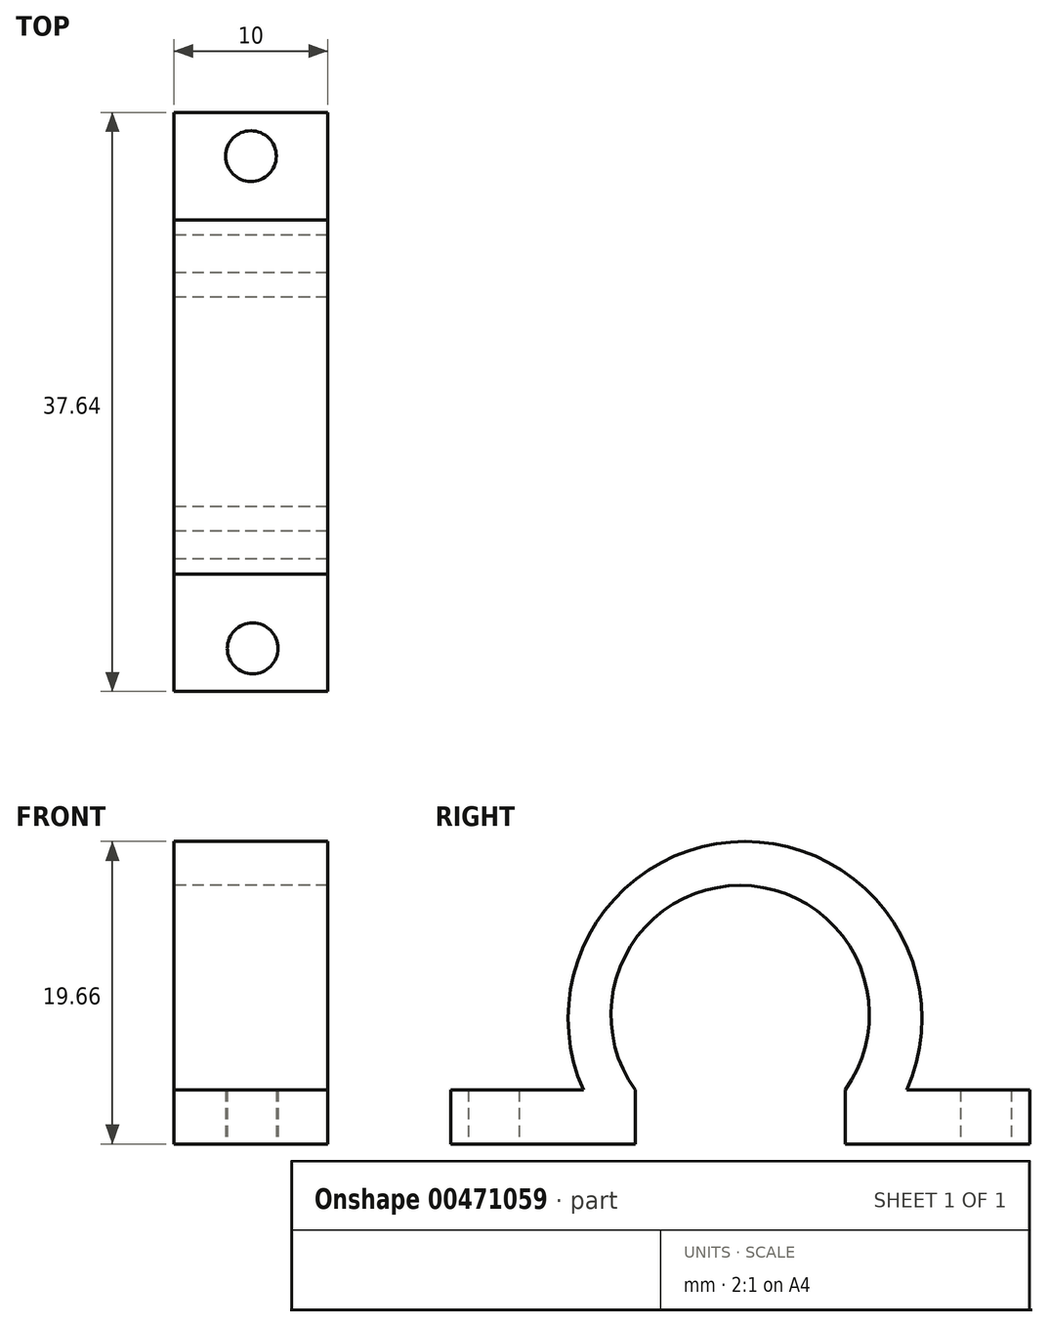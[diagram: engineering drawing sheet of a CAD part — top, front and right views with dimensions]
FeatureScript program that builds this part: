
annotation { "Feature Type Name" : "Feature", "Feature Type Description" : "" }
export const myFeature = defineFeature(function(context is Context, id is Id, definition is map)
    precondition{}
    {
        {
            var Q0;
            Q0=qCreatedBy(makeId("Right.planeOp"),FACE);
            var sketch = newSketch(context, id + "F0", { "sketchPlane" : qUnion([Q0])});
            skArc(sketch, "E0", {"start": v(-9.16, 19.45) * mm, "mid": v(-15.98, 32.75) * mm, "end": v(-22.8, 19.45) * mm});
            skLineSegment(sketch, "E1", {"start": v(-9.16, 15.95) * mm, "end": v(2.84, 15.95) * mm});
            skLineSegment(sketch, "E2", {"start": v(-34.8, 15.95) * mm, "end": v(-22.8, 15.95) * mm});
            skLineSegment(sketch, "E3", {"start": v(2.84, 15.95) * mm, "end": v(2.84, 19.45) * mm});
            skLineSegment(sketch, "E4", {"start": v(2.84, 19.45) * mm, "end": v(-9.16, 19.45) * mm});
            skLineSegment(sketch, "E5", {"start": v(-34.8, 19.45) * mm, "end": v(-34.8, 15.95) * mm});
            skLineSegment(sketch, "E6.trimOffspring", {"start": v(-22.8, 19.45) * mm, "end": v(-34.8, 19.45) * mm});
            skLineSegment(sketch, "E7", {"start": v(-22.8, 19.45) * mm, "end": v(-22.8, 15.95) * mm});
            skLineSegment(sketch, "E8", {"start": v(-9.16, 19.45) * mm, "end": v(-9.16, 15.95) * mm});
            skArc(sketch, "E9", {"start": v(-5.15, 19.45) * mm, "mid": v(-15.66, 35.6) * mm, "end": v(-26.18, 19.45) * mm});
            skSolve(sketch);
        }
        {
            var Q0;
            Q0 = qSketchRegion(id + "F0", true);
            extrude(context, id + "F1", {"entities" : qUnion([Q0]), "depth" : 10 * mm, "offsetDistance" : 25 * mm});
        }
        {
            var Q0;
            Q0=qCreatedBy(makeId("Top.planeOp"),FACE);
            var sketch = newSketch(context, id + "F2", { "sketchPlane" : qUnion([Q0])});
            skCircle(sketch, "E10", {"center": v(5.12, -32) * mm, "radius": 1.6 * mm});
            skCircle(sketch, "E11", {"center": v(5, 0) * mm, "radius": 1.6 * mm});
            skSolve(sketch);
        }
        {
            var Q0;
            Q0=sQuery(id+"F2.wireOp",VERTEX,"E10.center");
            var Q1;
            Q1=makeQuery(id+"F1.opExtrude","SWEPT_BODY",BODY,{"disambiguationData":[OSD([sQuery(id+"F0.wireOp",EDGE,"E0"),sQuery(id+"F0.wireOp",EDGE,"E1"),sQuery(id+"F0.wireOp",EDGE,"E2"),sQuery(id+"F0.wireOp",EDGE,"E3"),sQuery(id+"F0.wireOp",EDGE,"E4"),sQuery(id+"F0.wireOp",EDGE,"E5"),sQuery(id+"F0.wireOp",EDGE,"E6.trimOffspring"),sQuery(id+"F0.wireOp",EDGE,"E7"),sQuery(id+"F0.wireOp",EDGE,"E8"),sQuery(id+"F0.wireOp",EDGE,"E9")])]});
            hole(context, id + "F3", {"style" : HoleStyle.SIMPLE, "endStyle" : HoleEndStyle.THROUGH, "oppositeDirection" : true, "holeDiameter" : 3.3 * mm, "isTappedThrough" : true, "tappedDepth" : 12 * mm, "tapClearance" : 3, "locations" : qUnion([Q0]), "scope" : qUnion([Q1])});
        }
        {
            var Q0;
            Q0=sQuery(id+"F2.wireOp",VERTEX,"E11.center");
            var Q1;
            Q1=makeQuery(id+"F1.opExtrude","SWEPT_BODY",BODY,{"disambiguationData":[OSD([sQuery(id+"F0.wireOp",EDGE,"E0"),sQuery(id+"F0.wireOp",EDGE,"E1"),sQuery(id+"F0.wireOp",EDGE,"E2"),sQuery(id+"F0.wireOp",EDGE,"E3"),sQuery(id+"F0.wireOp",EDGE,"E4"),sQuery(id+"F0.wireOp",EDGE,"E5"),sQuery(id+"F0.wireOp",EDGE,"E6.trimOffspring"),sQuery(id+"F0.wireOp",EDGE,"E7"),sQuery(id+"F0.wireOp",EDGE,"E8"),sQuery(id+"F0.wireOp",EDGE,"E9")])]});
            hole(context, id + "F4", {"style" : HoleStyle.SIMPLE, "endStyle" : HoleEndStyle.THROUGH, "oppositeDirection" : true, "holeDiameter" : 3.3 * mm, "isTappedThrough" : true, "tappedDepth" : 12 * mm, "tapClearance" : 3, "locations" : qUnion([Q0]), "scope" : qUnion([Q1])});
        }
    });
